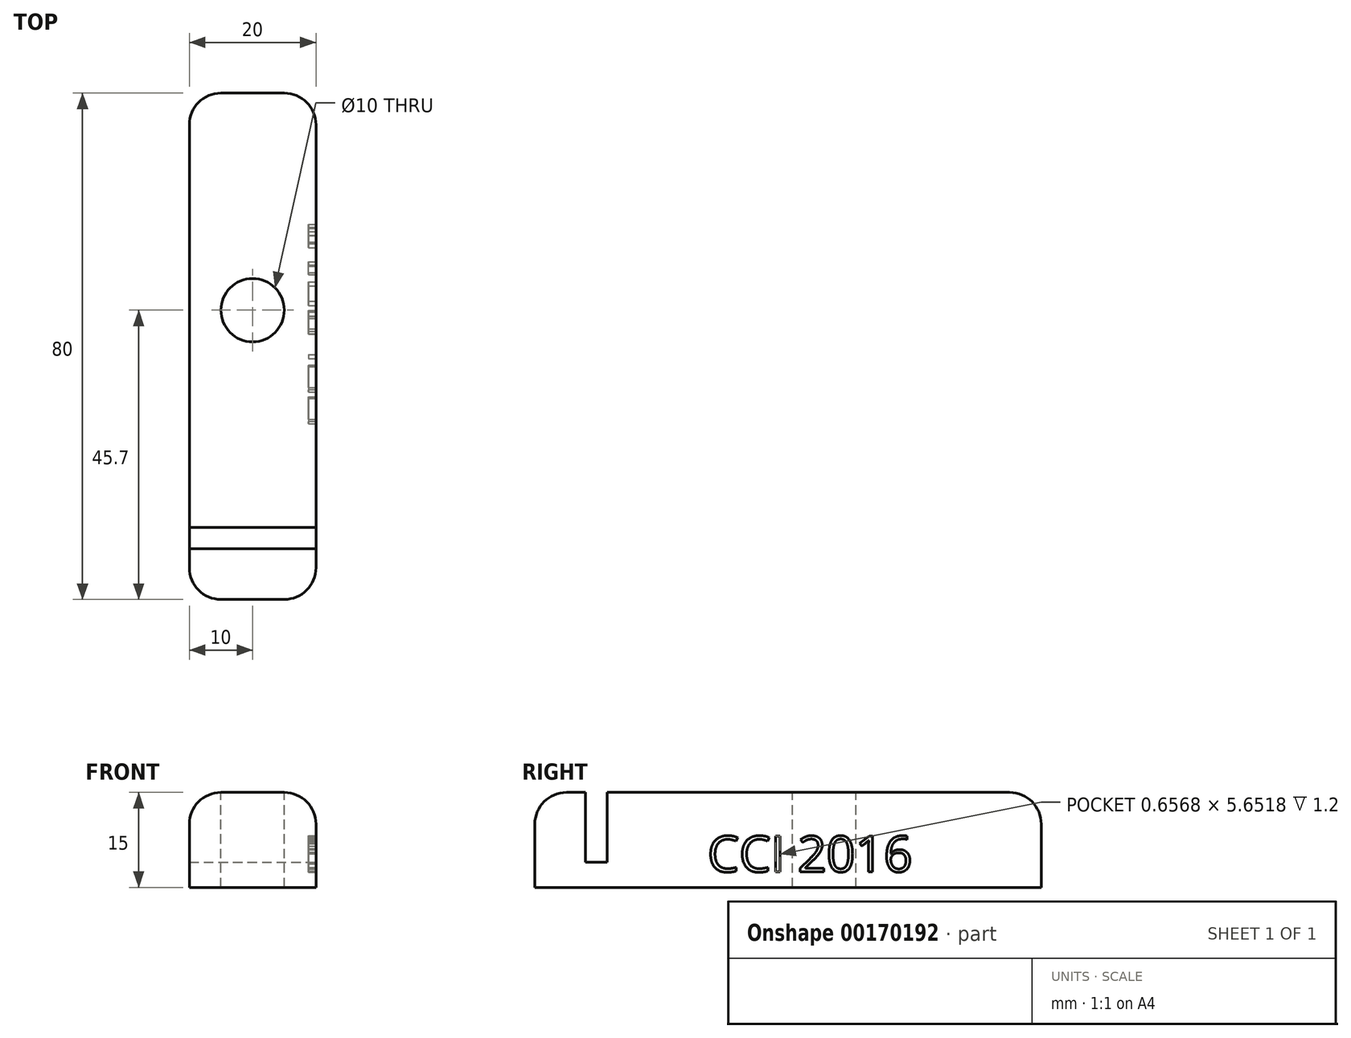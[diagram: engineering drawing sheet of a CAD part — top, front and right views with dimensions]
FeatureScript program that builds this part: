
annotation { "Feature Type Name" : "Feature", "Feature Type Description" : "" }
export const myFeature = defineFeature(function(context is Context, id is Id, definition is map)
    precondition{}
    {
        {
            var Q0;
            Q0=qCreatedBy(makeId("Top.planeOp"),FACE);
            var sketch = newSketch(context, id + "F0", { "sketchPlane" : qUnion([Q0])});
            skLineSegment(sketch, "E0.bottom", {"start": v(-10, -40) * mm, "end": v(10, -40) * mm});
            skLineSegment(sketch, "E0.top", {"start": v(-10, 40) * mm, "end": v(10, 40) * mm});
            skLineSegment(sketch, "E0.left", {"start": v(-10, -40) * mm, "end": v(-10, 40) * mm});
            skLineSegment(sketch, "E0.right", {"start": v(10, -40) * mm, "end": v(10, 40) * mm});
            skPoint(sketch, "E0.middle", {"position": v(0, 0) * mm});
            skSolve(sketch);
        }
        {
            var Q0;
            Q0=makeQuery(id+"F0.imprint","IMPRINT",FACE,{"disambiguationData":[TD([[makeQuery(id+"F0.imprint","IMPRINT",EDGE,{"derivedFrom":sQuery(id+"F0.wireOp",EDGE,"E0.bottom")}),1.0]])]});
            extrude(context, id + "F1", {"entities" : qUnion([Q0]), "depth" : 15 * mm});
        }
        {
            var Q0;
            Q0=makeQuery(id+"F1.opExtrude","CAP_FACE",FACE,{"disambiguationData":[OSD([sQuery(id+"F0.wireOp",EDGE,"E0.bottom"),sQuery(id+"F0.wireOp",EDGE,"E0.top"),sQuery(id+"F0.wireOp",EDGE,"E0.left"),sQuery(id+"F0.wireOp",EDGE,"E0.right")])],"isStart":false});
            var sketch = newSketch(context, id + "F2", { "sketchPlane" : qUnion([Q0])});
            skLineSegment(sketch, "E1", {"start": v(-10, -40) * mm, "end": v(-10, -32) * mm});
            skLineSegment(sketch, "E2", {"start": v(-10, -32) * mm, "end": v(10, -32) * mm});
            skLineSegment(sketch, "E3", {"start": v(10, -32) * mm, "end": v(10, -28.6) * mm});
            skLineSegment(sketch, "E4", {"start": v(10, -28.6) * mm, "end": v(-10, -28.6) * mm});
            skLineSegment(sketch, "E5", {"start": v(-10, -28.6) * mm, "end": v(-10, -32) * mm});
            skLineSegment(sketch, "E6", {"start": v(0, -28.6) * mm, "end": v(0, 40) * mm});
            skCircle(sketch, "E7", {"center": v(0, 5.7) * mm, "radius": 5 * mm});
            skLineSegment(sketch, "E8", {"start": v(0, 10.7) * mm, "end": v(0, 40) * mm});
            skCircle(sketch, "E9", {"center": v(0, 25.35) * mm, "radius": 5 * mm});
            skLineSegment(sketch, "E10", {"start": v(0, 0) * mm, "end": v(0, -28.6) * mm});
            skCircle(sketch, "E11", {"center": v(0, -14.3) * mm, "radius": 5 * mm});
            skSolve(sketch);
        }
        {
            var Q0;
            Q0=makeQuery(id+"F2.imprint","IMPRINT",FACE,{"disambiguationData":[TD([[makeQuery(id+"F2.imprint","IMPRINT",EDGE,{"derivedFrom":sQuery(id+"F2.wireOp",EDGE,"E2")}),1.0]])]});
            extrude(context, id + "F3", {"entities" : qUnion([Q0]), "operationType" : NewBodyOperationType.REMOVE, "oppositeDirection" : true, "depth" : 11 * mm});
        }
        {
            var Q0;
            {var subQ0=sQuery(id+"F2.wireOp",EDGE,"E9");var subQ1=sQuery(id+"F2.wireOp",EDGE,"E8");var subQ2=makeQuery(id+"F2.imprint","INTERSECT",VERTEX,{"disambiguationData":[OD(0.0)],"derivedFrom":[subQ1,subQ0]});Q0=makeQuery(id+"F2.imprint","IMPRINT",FACE,{"disambiguationData":[TD([[makeQuery(id+"F2.imprint","IMPRINT",EDGE,{"disambiguationData":[TD([[subQ2,-1.0]])],"derivedFrom":subQ1}),-1.0]])]});}
            var Q1;
            {var subQ0=sQuery(id+"F2.wireOp",EDGE,"E9");var subQ1=sQuery(id+"F2.wireOp",EDGE,"E8");var subQ2=makeQuery(id+"F2.imprint","INTERSECT",VERTEX,{"disambiguationData":[OD(0.0)],"derivedFrom":[subQ1,subQ0]});Q1=makeQuery(id+"F2.imprint","IMPRINT",FACE,{"disambiguationData":[TD([[makeQuery(id+"F2.imprint","IMPRINT",EDGE,{"disambiguationData":[TD([[subQ2,-1.0]])],"derivedFrom":subQ1}),1.0]])]});}
            var Q2;
            {var subQ0=sQuery(id+"F2.wireOp",EDGE,"E7");var subQ1=sQuery(id+"F2.wireOp",EDGE,"E6");var subQ3=makeQuery(id+"F2.imprint","INTERSECT",VERTEX,{"derivedFrom":[subQ1,subQ0]});Q2=makeQuery(id+"F2.imprint","IMPRINT",FACE,{"disambiguationData":[TD([[makeQuery(id+"F2.imprint","IMPRINT",EDGE,{"disambiguationData":[TD([[subQ3,-1.0]])],"derivedFrom":subQ1}),-1.0]])]});}
            var Q3;
            {var subQ0=sQuery(id+"F2.wireOp",EDGE,"E7");var subQ1=sQuery(id+"F2.wireOp",EDGE,"E6");var subQ3=makeQuery(id+"F2.imprint","INTERSECT",VERTEX,{"derivedFrom":[subQ1,subQ0]});Q3=makeQuery(id+"F2.imprint","IMPRINT",FACE,{"disambiguationData":[TD([[makeQuery(id+"F2.imprint","IMPRINT",EDGE,{"disambiguationData":[TD([[subQ3,-1.0]])],"derivedFrom":subQ1}),1.0]])]});}
            var Q4;
            {var subQ0=sQuery(id+"F2.wireOp",EDGE,"E11");var subQ1=sQuery(id+"F2.wireOp",EDGE,"E10");var subQ2=makeQuery(id+"F2.imprint","INTERSECT",VERTEX,{"disambiguationData":[OD(0.0)],"derivedFrom":[subQ1,subQ0]});Q4=makeQuery(id+"F2.imprint","IMPRINT",FACE,{"disambiguationData":[TD([[makeQuery(id+"F2.imprint","IMPRINT",EDGE,{"disambiguationData":[TD([[subQ2,-1.0]])],"derivedFrom":subQ1}),1.0]])]});}
            var Q5;
            {var subQ0=sQuery(id+"F2.wireOp",EDGE,"E11");var subQ1=sQuery(id+"F2.wireOp",EDGE,"E10");var subQ2=makeQuery(id+"F2.imprint","INTERSECT",VERTEX,{"disambiguationData":[OD(0.0)],"derivedFrom":[subQ1,subQ0]});Q5=makeQuery(id+"F2.imprint","IMPRINT",FACE,{"disambiguationData":[TD([[makeQuery(id+"F2.imprint","IMPRINT",EDGE,{"disambiguationData":[TD([[subQ2,-1.0]])],"derivedFrom":subQ1}),-1.0]])]});}
            extrude(context, id + "F4", {"entities" : qUnion([Q0, Q1, Q2, Q3, Q4, Q5]), "operationType" : NewBodyOperationType.REMOVE, "oppositeDirection" : true, "depth" : 25 * mm});
        }
        {
            var Q0;
            Q0=makeQuery(id+"F1.opExtrude","SWEPT_EDGE",EDGE,{"disambiguationData":[OSD([sQuery(id+"F0.wireOp",EDGE,"E0.top"),sQuery(id+"F0.wireOp",EDGE,"E0.left")])]});
            var Q1;
            Q1=makeQuery(id+"F1.opExtrude","SWEPT_EDGE",EDGE,{"disambiguationData":[OSD([sQuery(id+"F0.wireOp",EDGE,"E0.bottom"),sQuery(id+"F0.wireOp",EDGE,"E0.left")])]});
            var Q2;
            Q2=makeQuery(id+"F1.opExtrude","SWEPT_EDGE",EDGE,{"disambiguationData":[OSD([sQuery(id+"F0.wireOp",EDGE,"E0.bottom"),sQuery(id+"F0.wireOp",EDGE,"E0.right")])]});
            var Q3;
            Q3=makeQuery(id+"F1.opExtrude","SWEPT_EDGE",EDGE,{"disambiguationData":[OSD([sQuery(id+"F0.wireOp",EDGE,"E0.top"),sQuery(id+"F0.wireOp",EDGE,"E0.right")])]});
            fillet(context, id + "F5", {"entities" : qUnion([Q0, Q1, Q2, Q3]), "radius" : 5 * mm, "tangentPropagation" : true, "allowEdgeOverflow" : false});
        }
        {
            var Q0;
            {var subQ0=sQuery(id+"F0.wireOp",EDGE,"E0.left");var subQ1=sQuery(id+"F0.wireOp",EDGE,"E0.top");Q0=makeQuery(id+"F3.boolean.opBoolean","SPLIT",EDGE,{"disambiguationData":[TD([makeQuery(id+"F1.opExtrude","SWEPT_FACE",FACE,{"disambiguationData":[OSD([subQ1])]})])],"derivedFrom":makeQuery(id+"F1.opExtrude","CAP_EDGE",EDGE,{"disambiguationData":[OSD([subQ0])],"isStart":false})});}
            var Q1;
            {var subQ0=sQuery(id+"F0.wireOp",EDGE,"E0.bottom");var subQ1=sQuery(id+"F0.wireOp",EDGE,"E0.left");var subQ2=sQuery(id+"F0.wireOp",EDGE,"E0.right");Q1=makeQuery(id+"F5.opFillet","BLEND_EDGE",EDGE,{"blendedFrom":[makeQuery(id+"F1.opExtrude","SWEPT_EDGE",EDGE,{"disambiguationData":[OSD([subQ0,subQ2])]}),makeQuery(id+"F3.boolean.opBoolean","SPLIT",FACE,{"disambiguationData":[TD([makeQuery(id+"F1.opExtrude","SWEPT_FACE",FACE,{"disambiguationData":[OSD([subQ0])]})])],"derivedFrom":makeQuery(id+"F1.opExtrude","CAP_FACE",FACE,{"disambiguationData":[OSD([subQ0,sQuery(id+"F0.wireOp",EDGE,"E0.top"),subQ1,subQ2])],"isStart":false})})],"blendedInto":[makeQuery(id+"F3.boolean.opBoolean","SPLIT",FACE,{"disambiguationData":[TD([makeQuery(id+"F1.opExtrude","SWEPT_FACE",FACE,{"disambiguationData":[OSD([subQ0])]})])],"derivedFrom":makeQuery(id+"F1.opExtrude","CAP_FACE",FACE,{"disambiguationData":[OSD([subQ0,sQuery(id+"F0.wireOp",EDGE,"E0.top"),subQ1,subQ2])],"isStart":false})})]});}
            fillet(context, id + "F6", {"entities" : qUnion([Q0, Q1]), "radius" : 5 * mm, "tangentPropagation" : true, "allowEdgeOverflow" : false});
        }
        {
            var Q0;
            Q0=makeQuery(id+"F1.opExtrude","SWEPT_FACE",FACE,{"disambiguationData":[OSD([sQuery(id+"F0.wireOp",EDGE,"E0.right")])]});
            var sketch = newSketch(context, id + "F7", { "sketchPlane" : qUnion([Q0])});
            skText(sketch, "E12", { "text": "CCI 2016", "fontName": "OpenSans-Regular.ttf"});
            const initialGuessF7  = {"E12": [-0.01272, 0.00245, 1, 0, 0.0057]};
            skSetInitialGuess(sketch, initialGuessF7);
            skSolve(sketch);
        }
        {
            var Q0;
            Q0 = qSketchRegion(id + "F7", true);
            extrude(context, id + "F8", {"entities" : qUnion([Q0]), "operationType" : NewBodyOperationType.REMOVE, "oppositeDirection" : true, "depth" : 1.2 * mm});
        }
    });
